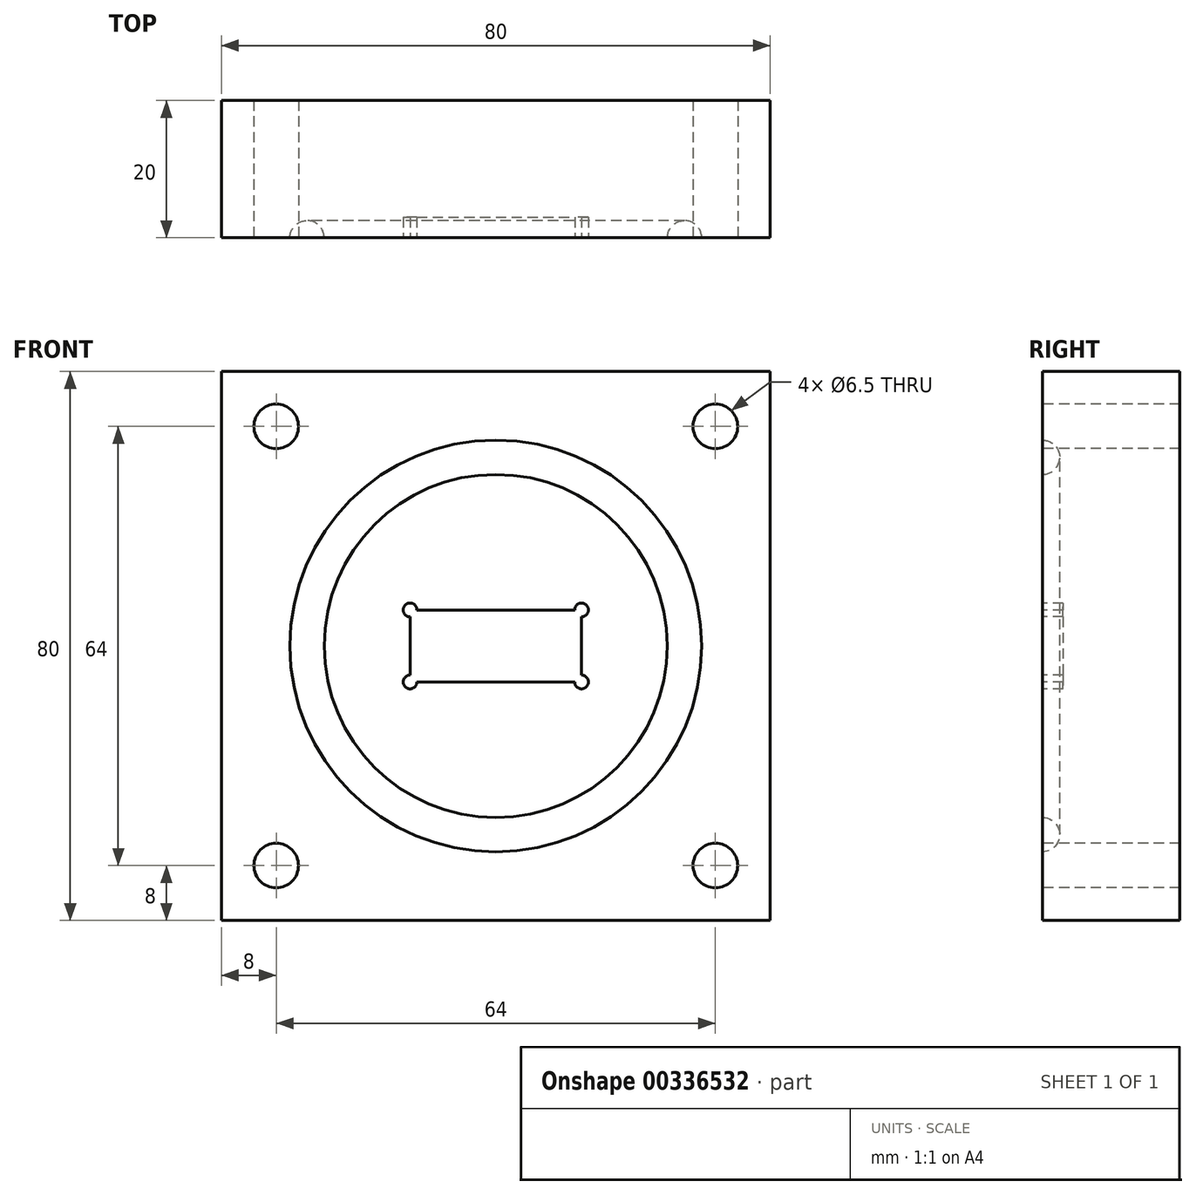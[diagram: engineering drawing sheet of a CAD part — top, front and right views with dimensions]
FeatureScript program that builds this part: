
annotation { "Feature Type Name" : "Feature", "Feature Type Description" : "" }
export const myFeature = defineFeature(function(context is Context, id is Id, definition is map)
    precondition{}
    {
        {
            assignVariable(context, id + "F0", {"name" : "Thickness", "anyValue" : 20});
        }
        {
            var Q0;
            Q0=qCreatedBy(makeId("Front.planeOp"),FACE);
            var sketch = newSketch(context, id + "F1", { "sketchPlane" : qUnion([Q0])});
            skLineSegment(sketch, "E0.bottom", {"start": v(0, 0) * mm, "end": v(80, 0) * mm});
            skLineSegment(sketch, "E0.top", {"start": v(0, 80) * mm, "end": v(80, 80) * mm});
            skLineSegment(sketch, "E0.left", {"start": v(0, 0) * mm, "end": v(0, 80) * mm});
            skLineSegment(sketch, "E0.right", {"start": v(80, 0) * mm, "end": v(80, 80) * mm});
            skSolve(sketch);
        }
        {
            var Q0;
            Q0=makeQuery(id+"F1.imprint","IMPRINT",FACE,{"disambiguationData":[TD([[makeQuery(id+"F1.imprint","IMPRINT",EDGE,{"derivedFrom":sQuery(id+"F1.wireOp",EDGE,"E0.bottom")}),1.0]])]});
            extrude(context, id + "F2", {"entities" : qUnion([Q0]), "depth" : (getVariable(context, 'Thickness')) * mm});
        }
        {
            assignVariable(context, id + "F3", {"name" : "G_thick", "anyValue" : 5});
        }
        {
            var Q0;
            Q0=makeQuery(id+"F2.opExtrude","CAP_FACE",FACE,{"disambiguationData":[OSD([sQuery(id+"F1.wireOp",EDGE,"E0.bottom"),sQuery(id+"F1.wireOp",EDGE,"E0.top"),sQuery(id+"F1.wireOp",EDGE,"E0.left"),sQuery(id+"F1.wireOp",EDGE,"E0.right")])],"isStart":false});
            var sketch = newSketch(context, id + "F4", { "sketchPlane" : qUnion([Q0])});
            skCircle(sketch, "E1", {"center": v(40, 40) * mm, "radius": 30 * mm});
            skCircle(sketch, "E2", {"center": v(40, 40) * mm, "radius": 25 * mm});
            skCircle(sketch, "E3", {"center": v(8, 72) * mm, "radius": 3.25 * mm});
            skCircle(sketch, "E4", {"center": v(8, 8) * mm, "radius": 3.25 * mm});
            skCircle(sketch, "E5", {"center": v(72, 8) * mm, "radius": 3.25 * mm});
            skCircle(sketch, "E6", {"center": v(72, 72) * mm, "radius": 3.25 * mm});
            skLineSegment(sketch, "E7.bottom", {"start": v(27.5, 45.25) * mm, "end": v(52.5, 45.25) * mm});
            skLineSegment(sketch, "E7.top", {"start": v(27.5, 34.75) * mm, "end": v(52.5, 34.75) * mm});
            skLineSegment(sketch, "E7.left", {"start": v(27.5, 45.25) * mm, "end": v(27.5, 34.75) * mm});
            skLineSegment(sketch, "E7.right", {"start": v(52.5, 45.25) * mm, "end": v(52.5, 34.75) * mm});
            skLineSegment(sketch, "E8", {"start": v(27.5, 40) * mm, "end": v(52.5, 40) * mm});
            skCircle(sketch, "E9", {"center": v(27.5, 45.25) * mm, "radius": 1 * mm});
            skCircle(sketch, "E10", {"center": v(52.5, 45.25) * mm, "radius": 1 * mm});
            skCircle(sketch, "E11", {"center": v(52.5, 34.75) * mm, "radius": 1 * mm});
            skCircle(sketch, "E12", {"center": v(27.5, 34.75) * mm, "radius": 1 * mm});
            skSolve(sketch);
        }
        {
            var Q0;
            Q0=makeQuery(id+"F4.imprint","IMPRINT",FACE,{"disambiguationData":[TD([[makeQuery(id+"F4.imprint","IMPRINT",EDGE,{"derivedFrom":sQuery(id+"F4.wireOp",EDGE,"E5")}),1.0]])]});
            var Q1;
            Q1=makeQuery(id+"F4.imprint","IMPRINT",FACE,{"disambiguationData":[TD([[makeQuery(id+"F4.imprint","IMPRINT",EDGE,{"derivedFrom":sQuery(id+"F4.wireOp",EDGE,"E4")}),1.0]])]});
            var Q2;
            Q2=makeQuery(id+"F4.imprint","IMPRINT",FACE,{"disambiguationData":[TD([[makeQuery(id+"F4.imprint","IMPRINT",EDGE,{"derivedFrom":sQuery(id+"F4.wireOp",EDGE,"E3")}),1.0]])]});
            var Q3;
            Q3=makeQuery(id+"F4.imprint","IMPRINT",FACE,{"disambiguationData":[TD([[makeQuery(id+"F4.imprint","IMPRINT",EDGE,{"derivedFrom":sQuery(id+"F4.wireOp",EDGE,"E6")}),1.0]])]});
            var Q4;
            Q4=sQuery(id+"F4.wireOp",EDGE,"E3");
            extrude(context, id + "F5", {"entities" : qUnion([Q0, Q1, Q2, Q3]), "operationType" : NewBodyOperationType.REMOVE, "surfaceEntities" : qUnion([Q4]), "endBound" : BoundingType.THROUGH_ALL, "oppositeDirection" : true, "depth" : 25 * mm});
        }
        {
            var Q0;
            Q0=makeQuery(id+"F4.imprint","IMPRINT",FACE,{"disambiguationData":[TD([[makeQuery(id+"F4.imprint","IMPRINT",EDGE,{"derivedFrom":sQuery(id+"F4.wireOp",EDGE,"E1")}),1.0]])]});
            var Q1;
            Q1=sQuery(id+"F4.wireOp",EDGE,"E1");
            var Q2;
            Q2=sQuery(id+"F4.wireOp",EDGE,"E2");
            extrude(context, id + "F6", {"entities" : qUnion([Q0]), "operationType" : NewBodyOperationType.REMOVE, "surfaceEntities" : qUnion([Q1, Q2]), "oppositeDirection" : true, "depth" : 2.5 * mm});
        }
        {
            var Q0;
            {var subQ0=sQuery(id+"F4.wireOp",EDGE,"E7.bottom");Q0=makeQuery(id+"F4.imprint","IMPRINT",FACE,{"disambiguationData":[TD([[makeQuery(id+"F4.imprint","IMPRINT",EDGE,{"derivedFrom":subQ0}),-1.0]])]});}
            var Q1;
            {var subQ0=sQuery(id+"F4.wireOp",EDGE,"E7.top");Q1=makeQuery(id+"F4.imprint","IMPRINT",FACE,{"disambiguationData":[TD([[makeQuery(id+"F4.imprint","IMPRINT",EDGE,{"derivedFrom":subQ0}),1.0]])]});}
            var Q2;
            {var subQ0=sQuery(id+"F4.wireOp",EDGE,"E7.left");var subQ1=sQuery(id+"F4.wireOp",EDGE,"E7.top");var subQ2=makeQuery(id+"F4.imprint","INTERSECT",VERTEX,{"derivedFrom":[subQ1,subQ0]});Q2=makeQuery(id+"F4.imprint","IMPRINT",FACE,{"disambiguationData":[TD([[makeQuery(id+"F4.imprint","IMPRINT",EDGE,{"disambiguationData":[TD([[subQ2,-1.0]])],"derivedFrom":subQ1}),-1.0]])]});}
            var Q3;
            {var subQ0=sQuery(id+"F4.wireOp",EDGE,"E7.right");var subQ1=sQuery(id+"F4.wireOp",EDGE,"E7.top");var subQ2=makeQuery(id+"F4.imprint","INTERSECT",VERTEX,{"derivedFrom":[subQ1,subQ0]});Q3=makeQuery(id+"F4.imprint","IMPRINT",FACE,{"disambiguationData":[TD([[makeQuery(id+"F4.imprint","IMPRINT",EDGE,{"disambiguationData":[TD([[subQ2,1.0]])],"derivedFrom":subQ1}),-1.0]])]});}
            var Q4;
            {var subQ0=sQuery(id+"F4.wireOp",EDGE,"E7.right");var subQ1=sQuery(id+"F4.wireOp",EDGE,"E7.bottom");var subQ2=makeQuery(id+"F4.imprint","INTERSECT",VERTEX,{"derivedFrom":[subQ1,subQ0]});Q4=makeQuery(id+"F4.imprint","IMPRINT",FACE,{"disambiguationData":[TD([[makeQuery(id+"F4.imprint","IMPRINT",EDGE,{"disambiguationData":[TD([[subQ2,1.0]])],"derivedFrom":subQ1}),1.0]])]});}
            var Q5;
            {var subQ0=sQuery(id+"F4.wireOp",EDGE,"E7.left");var subQ1=sQuery(id+"F4.wireOp",EDGE,"E7.bottom");var subQ2=makeQuery(id+"F4.imprint","INTERSECT",VERTEX,{"derivedFrom":[subQ1,subQ0]});Q5=makeQuery(id+"F4.imprint","IMPRINT",FACE,{"disambiguationData":[TD([[makeQuery(id+"F4.imprint","IMPRINT",EDGE,{"disambiguationData":[TD([[subQ2,-1.0]])],"derivedFrom":subQ1}),1.0]])]});}
            var Q6;
            {var subQ0=sQuery(id+"F4.wireOp",EDGE,"E8");Q6=makeQuery(id+"F4.imprint","IMPRINT",FACE,{"disambiguationData":[TD([[makeQuery(id+"F4.imprint","IMPRINT",EDGE,{"derivedFrom":subQ0}),1.0]])]});}
            var Q7;
            {var subQ0=sQuery(id+"F4.wireOp",EDGE,"E8");Q7=makeQuery(id+"F4.imprint","IMPRINT",FACE,{"disambiguationData":[TD([[makeQuery(id+"F4.imprint","IMPRINT",EDGE,{"derivedFrom":subQ0}),-1.0]])]});}
            extrude(context, id + "F7", {"entities" : qUnion([Q0, Q1, Q2, Q3, Q4, Q5, Q6, Q7]), "operationType" : NewBodyOperationType.REMOVE, "oppositeDirection" : true, "depth" : 3 * mm});
        }
        {
            var Q0;
            Q0=makeQuery(id+"F6.boolean.opBoolean","COPY",EDGE,{"derivedFrom":makeQuery(id+"F6.opExtrude","CAP_EDGE",EDGE,{"disambiguationData":[OSD([sQuery(id+"F4.wireOp",EDGE,"E2")])],"isStart":false})});
            fillet(context, id + "F8", {"entities" : qUnion([Q0]), "radius" : (getVariable(context, 'G_thick') / 2) * mm, "tangentPropagation" : true, "allowEdgeOverflow" : false});
        }
        {
            var Q0;
            Q0=makeQuery(id+"F6.boolean.opBoolean","COPY",EDGE,{"derivedFrom":makeQuery(id+"F6.opExtrude","CAP_EDGE",EDGE,{"disambiguationData":[OSD([sQuery(id+"F4.wireOp",EDGE,"E1")])],"isStart":false})});
            fillet(context, id + "F9", {"entities" : qUnion([Q0]), "radius" : (getVariable(context, 'G_thick') / 2) * mm, "tangentPropagation" : true, "allowEdgeOverflow" : false});
        }
    });
